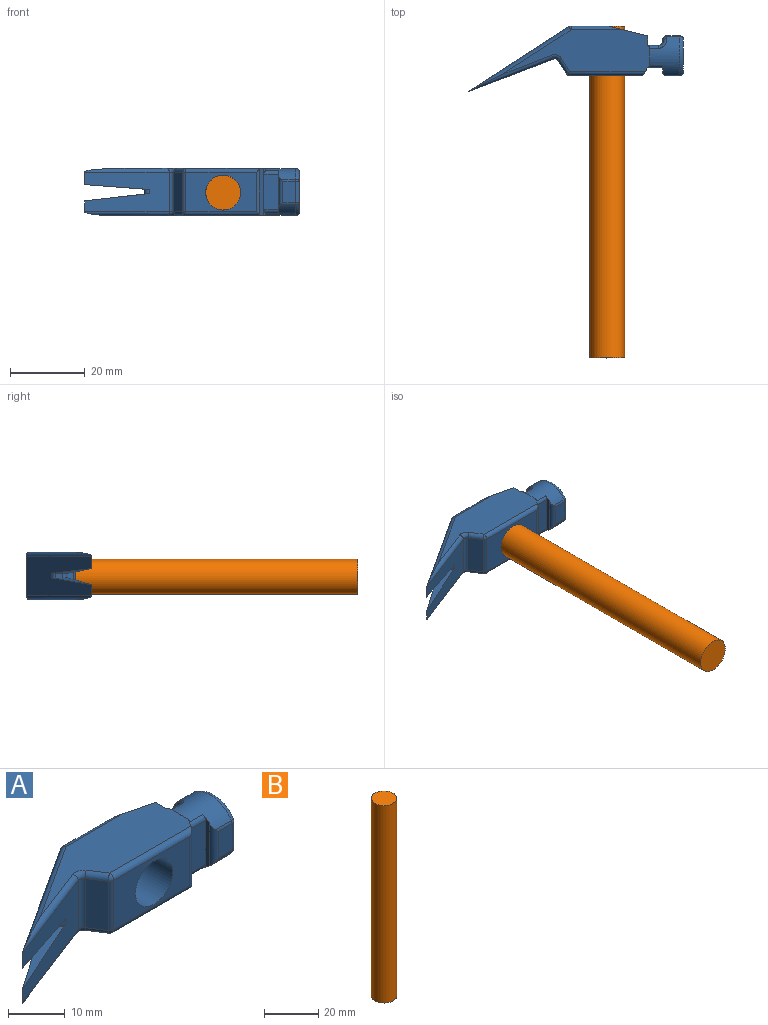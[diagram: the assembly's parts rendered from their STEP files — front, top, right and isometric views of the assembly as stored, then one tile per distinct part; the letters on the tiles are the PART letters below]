
ASSEMBLY  parts=2 mates=1
PART A: 76 faces, bbox 58x18.5x13.7 mm
  f0: plane 9.43x4mm, normal (0,-1,0), area 37.7mm2, adj f1,f11,f71,f73
  f1: plane 11.36x1.67mm, normal (-1,0,0), area 10.7mm2, adj f0,f22,f23,f26,f71,f73
  f2: plane 5.7x3.43mm, normal (0,-1,0), area 19.6mm2, adj f25,f26,f28,f29
  f3: plane 6.4x3.43mm, normal (0,1,0), area 22mm2, adj f34,f35,f39,f40
  f4: plane 7.47x0.48mm, normal (-1,0,0), area 3.3mm2, adj f40,f41,f45,f46
  f5: plane 10x2.93mm, normal (0,1,0), area 29.3mm2, adj f13,f42,f46,f49
  f6: plane 39.27x11.81mm, normal (0,0,1), area 282.1mm2, adj f11,f13,f14,f24,f38,f56,f61,f65
  f7: plane 39.27x11.81mm, normal (0,0,-1), area 282.1mm2, adj f11,f13,f14,f21,f47,f50,f51,f54
  f8: plane 26.87x17.39mm, normal (-0.54,0.84,0), area 283.1mm2, adj f9,f17,f18,f54,f60,f67,f74
  f9: plane 22.67x10.57mm, normal (0.36,-0.93,0), area 206mm2, adj f8,f17,f18,f59,f66,f69,f75
  f10: plane 18.91x10.57mm, normal (0,-1,0), area 131.4mm2, adj f20,f50,f52,f56,f57
  f11: plane 12.72x1.66mm, normal (0.84,-0.55,0), area 24.9mm2, adj f0,f6,f7,f50,f52,f56,f70,f72
  f12: plane 10.46x8.52mm, normal (1,0,0), area 77.8mm2, adj f29,f30,f33,f34
  f13: plane 12.7x2.61mm, normal (1,0,0), area 33.1mm2, adj f5,f6,f7,f14,f38,f47
  f14: plane 12.7x10.88mm, normal (0.23,0.97,0), area 104.8mm2, adj f6,f7,f13,f15,f20,f51,f61
  f15: plane 10.57x9.67mm, normal (0,1,0), area 68mm2, adj f14,f20,f51,f60,f61
  f16: plane 10.57x3.52mm, normal (-0.84,-0.54,0), area 44.3mm2, adj f57,f58,f65,f66
  f17: plane 17.42x10.67mm, normal (-0.08,0,-1), area 34mm2, adj f8,f9,f19,f74,f75
  f18: plane 17.44x10.69mm, normal (-0.11,0,0.99), area 34.1mm2, adj f8,f9,f19,f74,f75
  f19: plane 2.04x1.35mm, normal (-1,0,0), area 2.8mm2, adj f17,f18,f74,f75
  f20: cylinder r=4.67mm len=13.26mm, axis (0,-1,0), area 378.2mm2, adj f10,f14,f15
  f21: plane 4.14x0.55mm, normal (1,0,0), area 0.8mm2, adj f7,f22,f47,f72
  f22: cylinder r=6.29mm len=10.25mm, axis (1,0,0), area 67.4mm2, adj f1,f21,f26,f28,f33,f39,f45,f47
  f23: cylinder r=6.29mm len=10.25mm, axis (1,0,0), area 67.4mm2, adj f1,f24,f25,f26,f30,f35,f38,f41
  f24: plane 4.14x0.55mm, normal (1,0,0), area 0.8mm2, adj f6,f23,f38,f70
  f25: cylinder r=1.07mm len=4.01mm, axis (1,0,0), area 2.3mm2, adj f2,f23,f26,f27
  f26: cylinder r=1.07mm len=9.04mm, axis (0,0,-1), area 12.3mm2, adj f1,f2,f22,f23,f25,f28
  f27: sphere r=1.07mm, area 0.5mm2, adj f25,f29,f30
  f28: cylinder r=1.07mm len=4.01mm, axis (1,0,0), area 2.3mm2, adj f2,f22,f26,f31
  f29: cylinder r=1.07mm len=5.7mm, axis (0,0,-1), area 9.6mm2, adj f2,f12,f27,f31
  f30: torus R=5.23mm, axis (-1,0,0), area 18.9mm2, adj f12,f23,f27,f32
  f31: sphere r=1.07mm, area 0.5mm2, adj f28,f29,f33
  f32: sphere r=1.07mm, area 0.6mm2, adj f30,f34,f35
  f33: torus R=5.23mm, axis (-1,0,0), area 18.9mm2, adj f12,f22,f31,f36
  f34: cylinder r=1.07mm len=6.4mm, axis (0,0,-1), area 10.7mm2, adj f3,f12,f32,f36
  f35: cylinder r=1.07mm len=3.43mm, axis (1,0,0), area 2.4mm2, adj f3,f23,f32,f37
  f36: sphere r=1.07mm, area 0.6mm2, adj f33,f34,f39
  f37: sphere r=1.07mm, area 0.6mm2, adj f35,f40,f41
  f38: cylinder r=1.07mm len=1.35mm, axis (0,0,-1), area 0.6mm2, adj f6,f13,f23,f24,f42
  f39: cylinder r=1.07mm len=3.43mm, axis (1,0,0), area 2.4mm2, adj f3,f22,f36,f43
  f40: cylinder r=1.07mm len=6.4mm, axis (0,0,-1), area 10.7mm2, adj f3,f4,f37,f43
  f41: torus R=5.23mm, axis (1,0,0), area 1.4mm2, adj f4,f23,f37,f44
  f42: cylinder r=1.07mm len=2.93mm, axis (1,0,0), area 3.7mm2, adj f5,f23,f38,f44
  f43: sphere r=1.07mm, area 0.6mm2, adj f39,f40,f45
  f44: bspline ~3.15x2.82mm, area 4.3mm2, adj f23,f41,f42,f46
  f45: torus R=5.23mm, axis (1,0,0), area 1.4mm2, adj f4,f22,f43,f48
  f46: cylinder r=1.07mm len=10mm, axis (0,0,1), area 15.5mm2, adj f4,f5,f44,f48
  f47: cylinder r=1.07mm len=1.35mm, axis (0,0,-1), area 0.6mm2, adj f7,f13,f21,f22,f49
  f48: bspline ~3.08x2.75mm, area 4.3mm2, adj f22,f45,f46,f49
  f49: cylinder r=1.07mm len=2.93mm, axis (1,0,0), area 3.7mm2, adj f5,f22,f47,f48
  f50: cylinder r=1.07mm len=20.18mm, axis (1,0,0), area 32.8mm2, adj f7,f10,f11,f52,f53
  f51: cylinder r=1.07mm len=14.12mm, axis (-1,0,0), area 18.9mm2, adj f7,f14,f15,f55
  f52: cylinder r=1.07mm len=12.35mm, axis (0,0,-1), area 12.1mm2, adj f10,f11,f50,f56
  f53: sphere r=1.07mm, area 1.1mm2, adj f50,f57,f58
  f54: cylinder r=1.07mm len=27.45mm, axis (-0.84,-0.54,0), area 47.4mm2, adj f7,f8,f55,f59
  f55: sphere r=1.07mm, area 0.7mm2, adj f51,f54,f60
  f56: cylinder r=1.07mm len=20.18mm, axis (-1,0,0), area 32.8mm2, adj f6,f10,f11,f52,f62
  f57: cylinder r=1.07mm len=10.57mm, axis (0,0,-1), area 11.2mm2, adj f10,f16,f53,f62
  f58: cylinder r=1.07mm len=4.1mm, axis (0.54,-0.84,0), area 7mm2, adj f7,f16,f53,f63
  f59: cylinder r=1.07mm len=23.05mm, axis (0.93,0.36,0), area 34.5mm2, adj f7,f9,f54,f63
  f60: cylinder r=1.07mm len=10.57mm, axis (0,0,-1), area 6.5mm2, adj f8,f15,f55,f64
  f61: cylinder r=1.07mm len=14.12mm, axis (1,0,0), area 18.9mm2, adj f6,f14,f15,f64
  f62: sphere r=1.07mm, area 1.1mm2, adj f56,f57,f65
  f63: torus R=2.13mm, axis (0,0,1), area 3.3mm2, adj f7,f58,f59,f66
  f64: sphere r=1.07mm, area 0.7mm2, adj f60,f61,f67
  f65: cylinder r=1.07mm len=4.1mm, axis (-0.54,0.84,0), area 7mm2, adj f6,f16,f62,f68
  f66: cylinder r=1.07mm len=10.57mm, axis (0,0,1), area 15.4mm2, adj f9,f16,f63,f68
  f67: cylinder r=1.07mm len=27.45mm, axis (0.84,0.54,0), area 47.4mm2, adj f6,f8,f64,f69
  f68: torus R=2.13mm, axis (0,0,1), area 3.3mm2, adj f6,f65,f66,f69
  f69: cylinder r=1.07mm len=23.05mm, axis (-0.93,-0.36,0), area 34.5mm2, adj f6,f9,f67,f68
  f70: cylinder r=1.07mm len=1.63mm, axis (0,0,1), area 0.9mm2, adj f6,f11,f23,f24,f71
  f71: cylinder r=1.07mm len=4mm, axis (1,0,0), area 4.5mm2, adj f0,f1,f23,f70
  f72: cylinder r=1.07mm len=1.63mm, axis (0,0,1), area 0.9mm2, adj f7,f11,f21,f22,f73
  f73: cylinder r=1.07mm len=4mm, axis (1,0,0), area 4.5mm2, adj f0,f1,f22,f72
  f74: cylinder r=1.07mm len=1.35mm, axis (0,0,1), area 1.4mm2, adj f8,f17,f18,f19
  f75: cylinder r=1.07mm len=1.45mm, axis (0,0,-1), area 2.5mm2, adj f9,f17,f18,f19
PART B: 3 faces, bbox 9.3x9.3x88.9 mm
  f0: cylinder r=4.66mm len=88.9mm, axis (0,0,-1), area 2603.5mm2, adj f1,f2
  f1: plane 9.32x9.32mm, normal (0,0,1), area 68.2mm2, adj f0
  f2: plane 9.32x9.32mm, normal (0,0,-1), area 68.2mm2, adj f0
PLACE A t=(13.27,21.65,-22.72)mm
PLACE B rot(axis=(-1,0,0),90deg) t=(13.27,-54,-16.54)mm
MATE fastened B.f0 <-> A.f20  axis (0,-1,0) through (13.27,34.9,-16.54)mm
